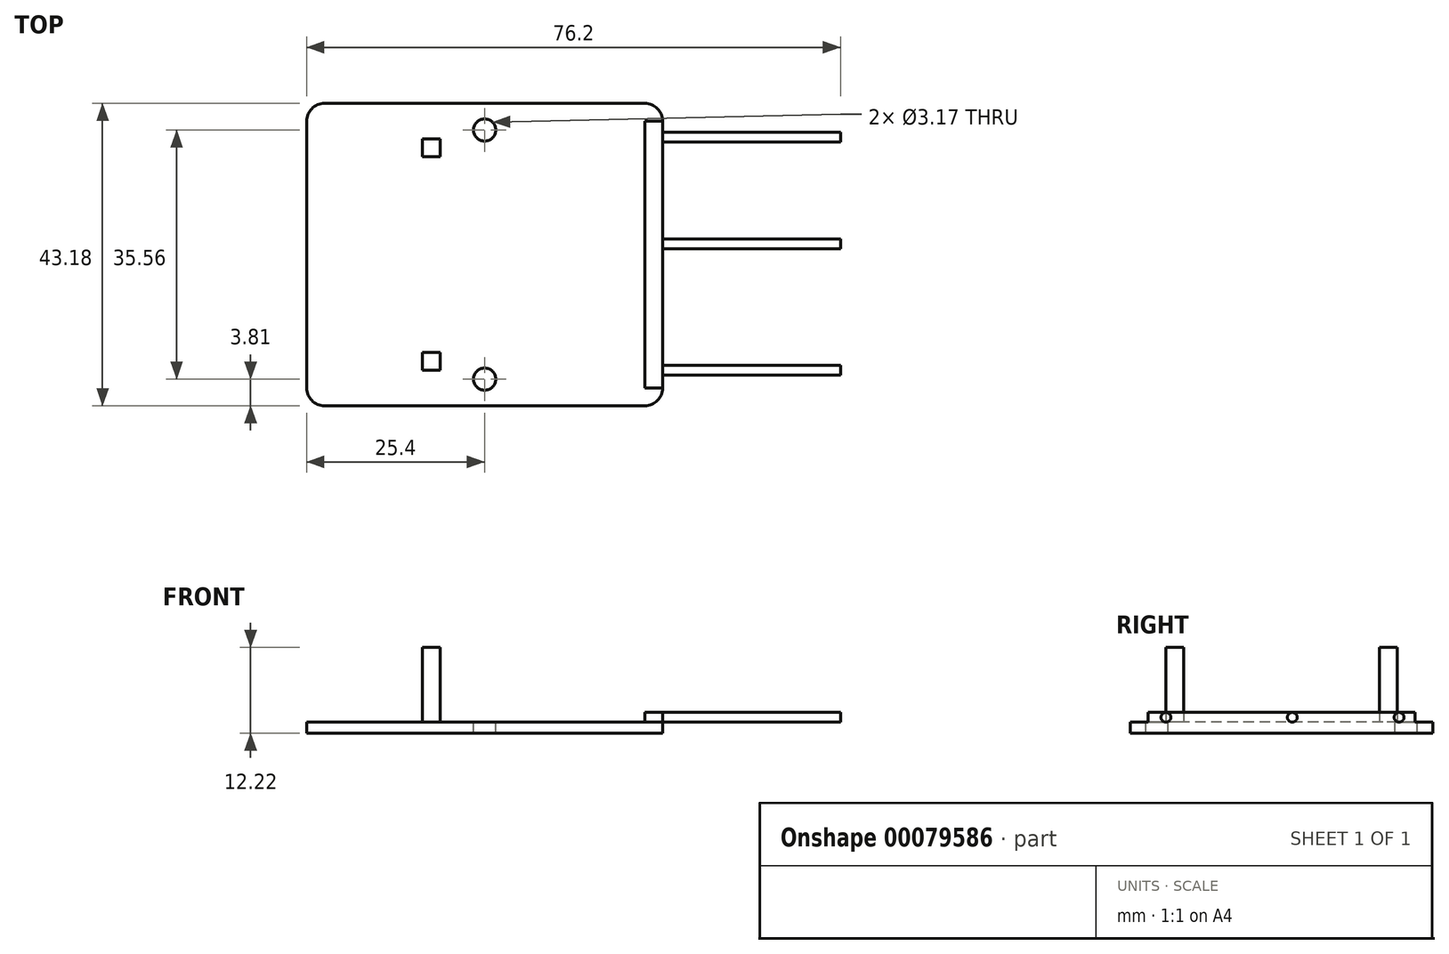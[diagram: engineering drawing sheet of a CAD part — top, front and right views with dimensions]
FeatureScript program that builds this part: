
annotation { "Feature Type Name" : "Feature", "Feature Type Description" : "" }
export const myFeature = defineFeature(function(context is Context, id is Id, definition is map)
    precondition{}
    {
        {
            var Q0;
            Q0=qCreatedBy(makeId("Top.planeOp"),FACE);
            var sketch = newSketch(context, id + "F0", { "sketchPlane" : qUnion([Q0])});
            skLineSegment(sketch, "E0.bottom", {"start": v(2.54, 0) * mm, "end": v(48.26, 0) * mm});
            skLineSegment(sketch, "E0.top", {"start": v(2.54, 43.18) * mm, "end": v(48.26, 43.18) * mm});
            skLineSegment(sketch, "E0.left", {"start": v(0, 2.54) * mm, "end": v(0, 40.64) * mm});
            skLineSegment(sketch, "E0.right", {"start": v(50.8, 2.54) * mm, "end": v(50.8, 40.64) * mm});
            skPoint(sketch, "E1.visualSharp", {"position": v(0, 43.18) * mm});
            skArc(sketch, "E1.filletArc", {"start": v(2.54, 43.18) * mm, "mid": v(0.74, 42.44) * mm, "end": v(0, 40.64) * mm});
            skPoint(sketch, "E2.visualSharp", {"position": v(50.8, 43.18) * mm});
            skArc(sketch, "E2.filletArc", {"start": v(50.8, 40.64) * mm, "mid": v(50.06, 42.44) * mm, "end": v(48.26, 43.18) * mm});
            skPoint(sketch, "E3.visualSharp", {"position": v(50.8, 0) * mm});
            skArc(sketch, "E3.filletArc", {"start": v(48.26, 0) * mm, "mid": v(50.06, 0.74) * mm, "end": v(50.8, 2.54) * mm});
            skPoint(sketch, "E4.visualSharp", {"position": v(0, 0) * mm});
            skArc(sketch, "E4.filletArc", {"start": v(0, 2.54) * mm, "mid": v(0.74, 0.74) * mm, "end": v(2.54, 0) * mm});
            skSolve(sketch);
        }
        {
            var Q0;
            Q0=makeQuery(id+"F0.imprint","IMPRINT",FACE,{"disambiguationData":[TD([[makeQuery(id+"F0.imprint","IMPRINT",EDGE,{"derivedFrom":sQuery(id+"F0.wireOp",EDGE,"E0.bottom")}),1.0]])]});
            extrude(context, id + "F1", {"entities" : qUnion([Q0]), "depth" : 1.55 * mm});
        }
        {
            var Q0;
            Q0=makeQuery(id+"F1.opExtrude","CAP_FACE",FACE,{"disambiguationData":[OSD([sQuery(id+"F0.wireOp",EDGE,"E0.bottom"),sQuery(id+"F0.wireOp",EDGE,"E0.top"),sQuery(id+"F0.wireOp",EDGE,"E0.left"),sQuery(id+"F0.wireOp",EDGE,"E0.right"),sQuery(id+"F0.wireOp",EDGE,"E1.filletArc"),sQuery(id+"F0.wireOp",EDGE,"E2.filletArc"),sQuery(id+"F0.wireOp",EDGE,"E3.filletArc"),sQuery(id+"F0.wireOp",EDGE,"E4.filletArc")])],"isStart":false});
            var sketch = newSketch(context, id + "F2", { "sketchPlane" : qUnion([Q0])});
            skCircle(sketch, "E5", {"center": v(25.4, 3.81) * mm, "radius": 1.59 * mm});
            skCircle(sketch, "E6", {"center": v(25.4, 39.37) * mm, "radius": 1.59 * mm});
            skSolve(sketch);
        }
        {
            var Q0;
            Q0=makeQuery(id+"F2.imprint","IMPRINT",FACE,{"disambiguationData":[TD([[makeQuery(id+"F2.imprint","IMPRINT",EDGE,{"derivedFrom":sQuery(id+"F2.wireOp",EDGE,"E6")}),1.0]])]});
            var Q1;
            Q1=makeQuery(id+"F2.imprint","IMPRINT",FACE,{"disambiguationData":[TD([[makeQuery(id+"F2.imprint","IMPRINT",EDGE,{"derivedFrom":sQuery(id+"F2.wireOp",EDGE,"E5")}),1.0]])]});
            extrude(context, id + "F3", {"entities" : qUnion([Q0, Q1]), "operationType" : NewBodyOperationType.REMOVE, "oppositeDirection" : true, "depth" : 25.4 * mm});
        }
        {
            var Q0;
            Q0=makeQuery(id+"F1.opExtrude","CAP_FACE",FACE,{"disambiguationData":[OSD([sQuery(id+"F0.wireOp",EDGE,"E0.bottom"),sQuery(id+"F0.wireOp",EDGE,"E0.top"),sQuery(id+"F0.wireOp",EDGE,"E0.left"),sQuery(id+"F0.wireOp",EDGE,"E0.right"),sQuery(id+"F0.wireOp",EDGE,"E1.filletArc"),sQuery(id+"F0.wireOp",EDGE,"E2.filletArc"),sQuery(id+"F0.wireOp",EDGE,"E3.filletArc"),sQuery(id+"F0.wireOp",EDGE,"E4.filletArc")])],"isStart":false});
            var sketch = newSketch(context, id + "F4", { "sketchPlane" : qUnion([Q0])});
            skLineSegment(sketch, "E7.bottom", {"start": v(16.51, 7.62) * mm, "end": v(19.05, 7.62) * mm});
            skLineSegment(sketch, "E7.top", {"start": v(16.51, 5.08) * mm, "end": v(19.05, 5.08) * mm});
            skLineSegment(sketch, "E7.left", {"start": v(16.51, 7.62) * mm, "end": v(16.51, 5.08) * mm});
            skLineSegment(sketch, "E7.right", {"start": v(19.05, 7.62) * mm, "end": v(19.05, 5.08) * mm});
            skLineSegment(sketch, "E8.bottom", {"start": v(16.51, 38.1) * mm, "end": v(19.05, 38.1) * mm});
            skLineSegment(sketch, "E8.top", {"start": v(16.51, 35.56) * mm, "end": v(19.05, 35.56) * mm});
            skLineSegment(sketch, "E8.left", {"start": v(16.51, 38.1) * mm, "end": v(16.51, 35.56) * mm});
            skLineSegment(sketch, "E8.right", {"start": v(19.05, 38.1) * mm, "end": v(19.05, 35.56) * mm});
            skSolve(sketch);
        }
        {
            var Q0;
            Q0=makeQuery(id+"F4.imprint","IMPRINT",FACE,{"disambiguationData":[TD([[makeQuery(id+"F4.imprint","IMPRINT",EDGE,{"derivedFrom":sQuery(id+"F4.wireOp",EDGE,"E8.bottom")}),-1.0]])]});
            var Q1;
            Q1=makeQuery(id+"F4.imprint","IMPRINT",FACE,{"disambiguationData":[TD([[makeQuery(id+"F4.imprint","IMPRINT",EDGE,{"derivedFrom":sQuery(id+"F4.wireOp",EDGE,"E7.bottom")}),-1.0]])]});
            extrude(context, id + "F5", {"entities" : qUnion([Q0, Q1]), "operationType" : NewBodyOperationType.ADD, "depth" : 10.67 * mm});
        }
        {
            var Q0;
            Q0=makeQuery(id+"F1.opExtrude","SWEPT_FACE",FACE,{"disambiguationData":[OSD([sQuery(id+"F0.wireOp",EDGE,"E0.right")])]});
            var sketch = newSketch(context, id + "F6", { "sketchPlane" : qUnion([Q0])});
            skCircle(sketch, "E9", {"center": v(5.08, 2.25) * mm, "radius": 0.7 * mm});
            skCircle(sketch, "E10", {"center": v(23.11, 2.25) * mm, "radius": 0.7 * mm});
            skCircle(sketch, "E11", {"center": v(38.35, 2.25) * mm, "radius": 0.7 * mm});
            skSolve(sketch);
        }
        {
            var Q0;
            Q0=makeQuery(id+"F1.opExtrude","CAP_FACE",FACE,{"disambiguationData":[OSD([sQuery(id+"F0.wireOp",EDGE,"E0.bottom"),sQuery(id+"F0.wireOp",EDGE,"E0.top"),sQuery(id+"F0.wireOp",EDGE,"E0.left"),sQuery(id+"F0.wireOp",EDGE,"E0.right"),sQuery(id+"F0.wireOp",EDGE,"E1.filletArc"),sQuery(id+"F0.wireOp",EDGE,"E2.filletArc"),sQuery(id+"F0.wireOp",EDGE,"E3.filletArc"),sQuery(id+"F0.wireOp",EDGE,"E4.filletArc")])],"isStart":false});
            var sketch = newSketch(context, id + "F7", { "sketchPlane" : qUnion([Q0])});
            skLineSegment(sketch, "E12.bottom", {"start": v(50.8, 40.64) * mm, "end": v(48.26, 40.64) * mm});
            skLineSegment(sketch, "E12.top", {"start": v(50.8, 2.54) * mm, "end": v(48.26, 2.54) * mm});
            skLineSegment(sketch, "E12.left", {"start": v(50.8, 40.64) * mm, "end": v(50.8, 2.54) * mm});
            skLineSegment(sketch, "E12.right", {"start": v(48.26, 40.64) * mm, "end": v(48.26, 2.54) * mm});
            skSolve(sketch);
        }
        {
            var Q0;
            Q0=makeQuery(id+"F7.imprint","IMPRINT",FACE,{"disambiguationData":[TD([[makeQuery(id+"F7.imprint","IMPRINT",EDGE,{"derivedFrom":sQuery(id+"F7.wireOp",EDGE,"E12.bottom")}),1.0]])]});
            extrude(context, id + "F8", {"entities" : qUnion([Q0]), "operationType" : NewBodyOperationType.ADD, "depth" : 1.4 * mm});
        }
        {
            var Q0;
            Q0=makeQuery(id+"F6.imprint","IMPRINT",FACE,{"disambiguationData":[TD([[makeQuery(id+"F6.imprint","IMPRINT",EDGE,{"derivedFrom":sQuery(id+"F6.wireOp",EDGE,"E9")}),1.0]])]});
            var Q1;
            Q1=makeQuery(id+"F6.imprint","IMPRINT",FACE,{"disambiguationData":[TD([[makeQuery(id+"F6.imprint","IMPRINT",EDGE,{"derivedFrom":sQuery(id+"F6.wireOp",EDGE,"E10")}),1.0]])]});
            var Q2;
            Q2=makeQuery(id+"F6.imprint","IMPRINT",FACE,{"disambiguationData":[TD([[makeQuery(id+"F6.imprint","IMPRINT",EDGE,{"derivedFrom":sQuery(id+"F6.wireOp",EDGE,"E11")}),1.0]])]});
            extrude(context, id + "F9", {"entities" : qUnion([Q0, Q1, Q2]), "operationType" : NewBodyOperationType.ADD, "depth" : 25.4 * mm});
        }
    });
